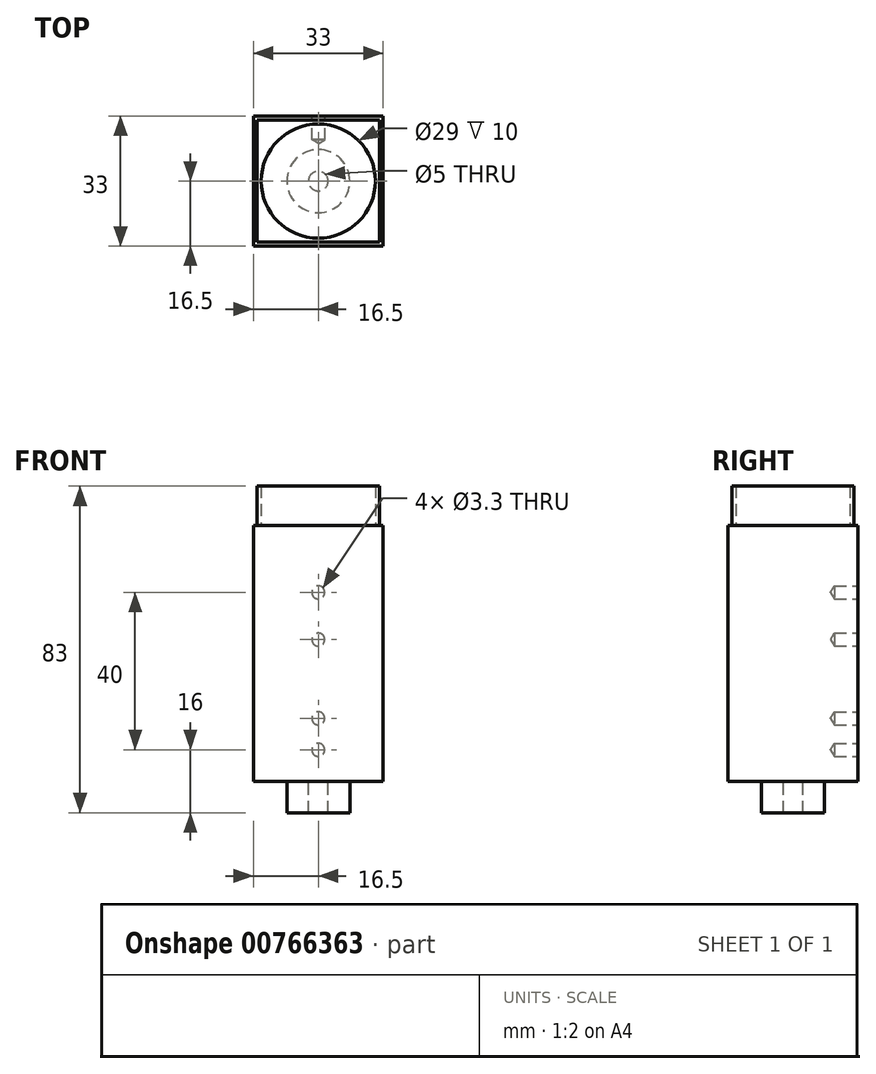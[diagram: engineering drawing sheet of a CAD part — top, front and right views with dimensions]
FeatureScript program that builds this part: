
annotation { "Feature Type Name" : "Feature", "Feature Type Description" : "" }
export const myFeature = defineFeature(function(context is Context, id is Id, definition is map)
    precondition{}
    {
        {
            var Q0;
            Q0=qCreatedBy(makeId("Top.planeOp"),FACE);
            var sketch = newSketch(context, id + "F0", { "sketchPlane" : qUnion([Q0])});
            skLineSegment(sketch, "E0.bottom", {"start": v(16.5, -16.5) * mm, "end": v(-16.5, -16.5) * mm});
            skLineSegment(sketch, "E0.top", {"start": v(16.5, 16.5) * mm, "end": v(-16.5, 16.5) * mm});
            skLineSegment(sketch, "E0.left", {"start": v(16.5, -16.5) * mm, "end": v(16.5, 16.5) * mm});
            skLineSegment(sketch, "E0.right", {"start": v(-16.5, -16.5) * mm, "end": v(-16.5, 16.5) * mm});
            skPoint(sketch, "E0.middle", {"position": v(0, 0) * mm});
            skSolve(sketch);
        }
        {
            var Q0;
            Q0 = qSketchRegion(id + "F0", true);
            extrude(context, id + "F1", {"entities" : qUnion([Q0]), "endBound" : BoundingType.SYMMETRIC, "depth" : 65 * mm, "offsetDistance" : 25 * mm});
        }
        {
            var Q0;
            Q0=makeQuery(id+"F1.opExtrude","CAP_FACE",FACE,{"disambiguationData":[OSD([sQuery(id+"F0.wireOp",EDGE,"E0.bottom"),sQuery(id+"F0.wireOp",EDGE,"E0.top"),sQuery(id+"F0.wireOp",EDGE,"E0.left"),sQuery(id+"F0.wireOp",EDGE,"E0.right")])],"isStart":true});
            var sketch = newSketch(context, id + "F2", { "sketchPlane" : qUnion([Q0])});
            skCircle(sketch, "E1", {"center": v(0, 0) * mm, "radius": 8 * mm});
            skCircle(sketch, "E2", {"center": v(0, 0) * mm, "radius": 2.5 * mm});
            skSolve(sketch);
        }
        {
            var Q0;
            Q0=makeQuery(id+"F2.imprint","IMPRINT",FACE,{"disambiguationData":[TD([[makeQuery(id+"F2.imprint","IMPRINT",EDGE,{"derivedFrom":sQuery(id+"F2.wireOp",EDGE,"E1")}),1.0]])]});
            extrude(context, id + "F3", {"entities" : qUnion([Q0]), "depth" : 8 * mm, "offsetDistance" : 25 * mm});
        }
        {
            var Q0;
            Q0=makeQuery(id+"F1.opExtrude","CAP_FACE",FACE,{"disambiguationData":[OSD([sQuery(id+"F0.wireOp",EDGE,"E0.bottom"),sQuery(id+"F0.wireOp",EDGE,"E0.top"),sQuery(id+"F0.wireOp",EDGE,"E0.left"),sQuery(id+"F0.wireOp",EDGE,"E0.right")])],"isStart":false});
            var sketch = newSketch(context, id + "F4", { "sketchPlane" : qUnion([Q0])});
            skCircle(sketch, "E3", {"center": v(0, 0) * mm, "radius": 14.5 * mm});
            skLineSegment(sketch, "E4.0", {"start": v(15.5, -15.5) * mm, "end": v(15.5, 15.5) * mm});
            skLineSegment(sketch, "E4.1", {"start": v(15.5, -15.5) * mm, "end": v(-15.5, -15.5) * mm});
            skLineSegment(sketch, "E4.2", {"start": v(-15.5, -15.5) * mm, "end": v(-15.5, 15.5) * mm});
            skLineSegment(sketch, "E4.3", {"start": v(15.5, 15.5) * mm, "end": v(-15.5, 15.5) * mm});
            skSolve(sketch);
        }
        {
            var Q0;
            Q0=makeQuery(id+"F4.imprint","IMPRINT",FACE,{"disambiguationData":[TD([[makeQuery(id+"F4.imprint","IMPRINT",EDGE,{"derivedFrom":sQuery(id+"F4.wireOp",EDGE,"E3")}),-1.0]])]});
            extrude(context, id + "F5", {"entities" : qUnion([Q0]), "depth" : 10 * mm, "offsetDistance" : 25 * mm});
        }
        {
            var Q0;
            Q0=makeQuery(id+"F1.opExtrude","SWEPT_FACE",FACE,{"disambiguationData":[OSD([sQuery(id+"F0.wireOp",EDGE,"E0.top")])]});
            var sketch = newSketch(context, id + "F6", { "sketchPlane" : qUnion([Q0])});
            skLineSegment(sketch, "E5", {"start": v(0, 15.5) * mm, "end": v(0, -24.5) * mm});
            skCircle(sketch, "E6", {"center": v(0, -24.5) * mm, "radius": 2.7 * mm});
            skCircle(sketch, "E7", {"center": v(0, -16.5) * mm, "radius": 2.7 * mm});
            skCircle(sketch, "E8", {"center": v(0, 3.5) * mm, "radius": 2.7 * mm});
            skCircle(sketch, "E9", {"center": v(0, 15.5) * mm, "radius": 2.7 * mm});
            skSolve(sketch);
        }
        {
            var Q0;
            Q0=sQuery(id+"F6.wireOp",VERTEX,"E9.center");
            var Q1;
            Q1=sQuery(id+"F6.wireOp",VERTEX,"E8.center");
            var Q2;
            Q2=sQuery(id+"F6.wireOp",VERTEX,"E7.center");
            var Q3;
            Q3=sQuery(id+"F6.wireOp",VERTEX,"E6.center");
            var Q4;
            Q4=makeQuery(id+"F1.opExtrude","SWEPT_BODY",BODY,{"disambiguationData":[OSD([sQuery(id+"F0.wireOp",EDGE,"E0.bottom"),sQuery(id+"F0.wireOp",EDGE,"E0.top"),sQuery(id+"F0.wireOp",EDGE,"E0.left"),sQuery(id+"F0.wireOp",EDGE,"E0.right")])]});
            hole(context, id + "F7", {"style" : HoleStyle.SIMPLE, "endStyle" : HoleEndStyle.BLIND, "standardTappedOrClearance" : lookupTablePath({ "standard" : "ISO", "fit" : "Normal", "size" : "M3", "type" : "Clearance" }), "standardBlindInLast" : lookupTablePath({ "fit" : "Standard", "standard" : "ISO", "size" : "M3", "type" : "Clearance" }), "holeDiameter" : 3.3 * mm, "majorDiameter" : 5 * mm, "holeDepth" : 6 * mm, "tappedDepth" : 7.6 * mm, "tapClearance" : 3, "locations" : qUnion([Q0, Q1, Q2, Q3]), "scope" : qUnion([Q4])});
        }
    });
